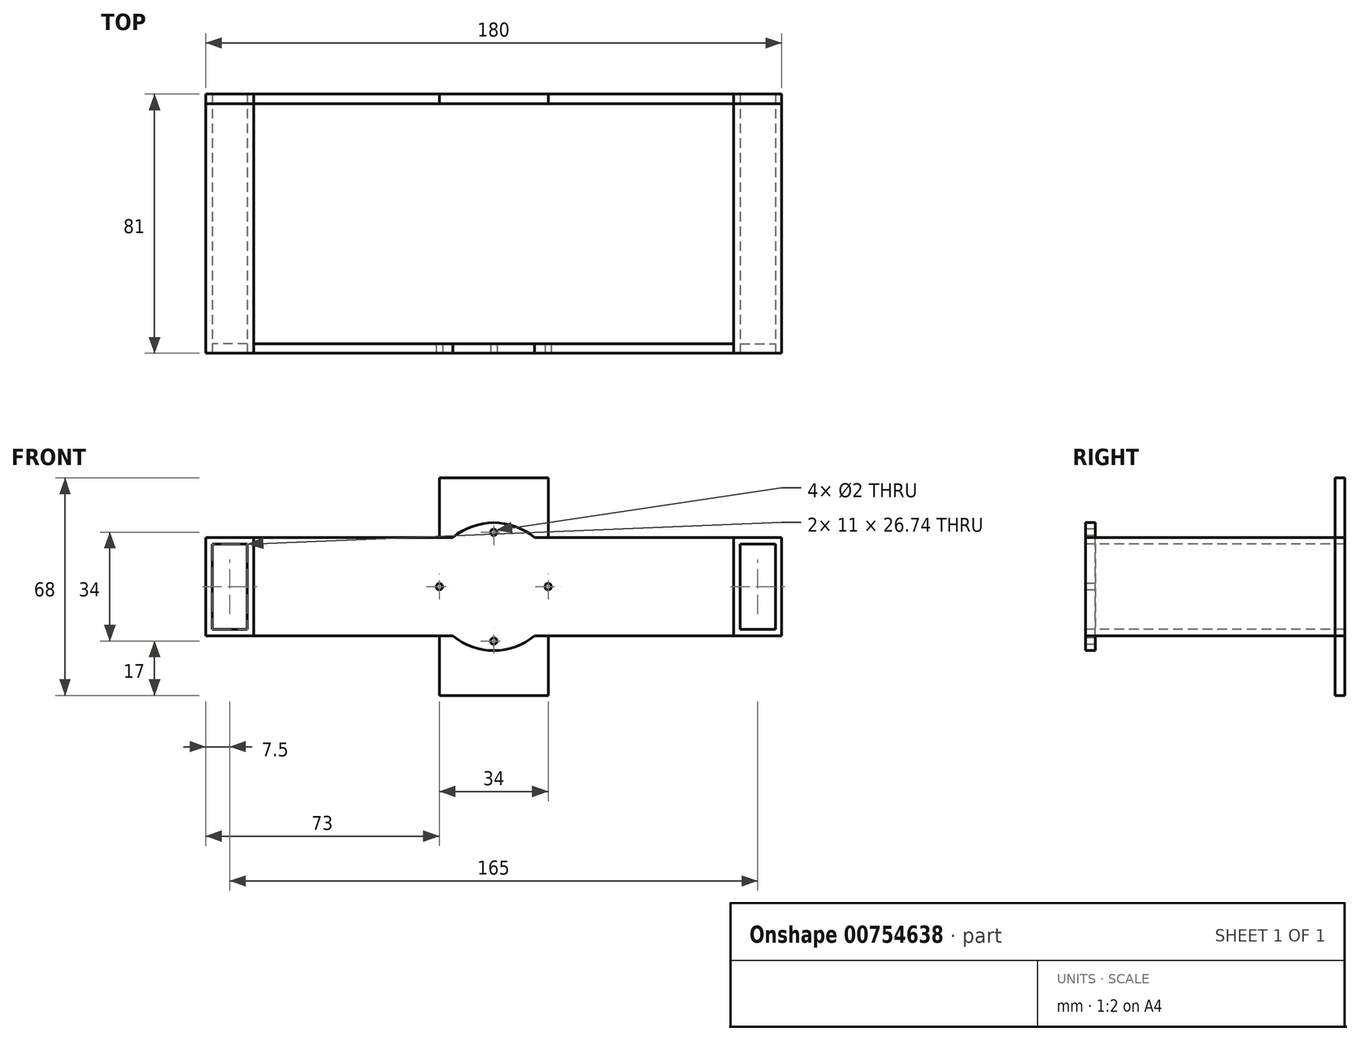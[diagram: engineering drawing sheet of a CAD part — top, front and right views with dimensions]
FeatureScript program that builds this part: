
annotation { "Feature Type Name" : "Feature", "Feature Type Description" : "" }
export const myFeature = defineFeature(function(context is Context, id is Id, definition is map)
    precondition{}
    {
        {
            var Q0;
            Q0=qCreatedBy(makeId("Front.planeOp"),FACE);
            var sketch = newSketch(context, id + "F0", { "sketchPlane" : qUnion([Q0])});
            skCircle(sketch, "E0", {"center": v(0, 0) * mm, "radius": 17 * mm, "construction": true});
            skCircle(sketch, "E1", {"center": v(0, 0) * mm, "radius": 20 * mm});
            skLineSegment(sketch, "E2", {"start": v(0, 0) * mm, "end": v(-69, 0) * mm});
            skLineSegment(sketch, "E3", {"start": v(0, 0) * mm, "end": v(69, 0) * mm});
            skLineSegment(sketch, "E4", {"start": v(-69, 0) * mm, "end": v(-75, 0) * mm});
            skLineSegment(sketch, "E5", {"start": v(69, 0) * mm, "end": v(75, 0) * mm});
            skPoint(sketch, "E6", {"position": v(0, 17) * mm});
            skCircle(sketch, "E7", {"center": v(0, 17) * mm, "radius": 1 * mm});
            skCircle(sketch, "E8.1.0", {"center": v(-17, 0) * mm, "radius": 1 * mm});
            skCircle(sketch, "E8.2.0", {"center": v(0, -17) * mm, "radius": 1 * mm});
            skCircle(sketch, "E8.3.0", {"center": v(17, 0) * mm, "radius": 1 * mm});
            skLineSegment(sketch, "E9", {"start": v(-75, 0) * mm, "end": v(-75, 15.37) * mm});
            skLineSegment(sketch, "E10.MirrorCS", {"start": v(-75, 0) * mm, "end": v(-75, -15.37) * mm});
            skLineSegment(sketch, "E11.MirrorCS", {"start": v(75, 0) * mm, "end": v(75, 15.37) * mm});
            skLineSegment(sketch, "E12.MirrorCS", {"start": v(75, 0) * mm, "end": v(75, -15.37) * mm});
            skLineSegment(sketch, "E13", {"start": v(-75, 15.37) * mm, "end": v(-12.8, 15.37) * mm});
            skLineSegment(sketch, "E14.MirrorCS", {"start": v(-75, -15.37) * mm, "end": v(-12.8, -15.37) * mm});
            skLineSegment(sketch, "E15.MirrorCS", {"start": v(75, 15.37) * mm, "end": v(12.8, 15.37) * mm});
            skLineSegment(sketch, "E16.MirrorCS", {"start": v(75, -15.37) * mm, "end": v(12.8, -15.37) * mm});
            skLineSegment(sketch, "E17", {"start": v(-75, -15.37) * mm, "end": v(-90, -15.37) * mm});
            skLineSegment(sketch, "E18.bottom", {"start": v(-75, 15.37) * mm, "end": v(-90, 15.37) * mm});
            skLineSegment(sketch, "E18.left", {"start": v(-75, 15.37) * mm, "end": v(-75, -15.37) * mm});
            skLineSegment(sketch, "E18.right", {"start": v(-90, 15.37) * mm, "end": v(-90, -15.37) * mm});
            skLineSegment(sketch, "E19.MirrorCS", {"start": v(90, 15.37) * mm, "end": v(90, -15.37) * mm});
            skLineSegment(sketch, "E20.MirrorCS", {"start": v(75, 15.37) * mm, "end": v(90, 15.37) * mm});
            skLineSegment(sketch, "E21.MirrorCS", {"start": v(75, -15.37) * mm, "end": v(90, -15.37) * mm});
            skLineSegment(sketch, "E22.0", {"start": v(-88, 13.37) * mm, "end": v(-88, -13.37) * mm});
            skLineSegment(sketch, "E22.1", {"start": v(-77, 13.37) * mm, "end": v(-88, 13.37) * mm});
            skLineSegment(sketch, "E22.2", {"start": v(-77, -13.37) * mm, "end": v(-88, -13.37) * mm});
            skLineSegment(sketch, "E22.3", {"start": v(-77, 0) * mm, "end": v(-77, -13.37) * mm});
            skLineSegment(sketch, "E22.4", {"start": v(-77, 0) * mm, "end": v(-77, 13.37) * mm});
            skLineSegment(sketch, "E23.MirrorCS", {"start": v(77, 13.37) * mm, "end": v(88, 13.37) * mm});
            skLineSegment(sketch, "E24.MirrorCS", {"start": v(77, -13.37) * mm, "end": v(88, -13.37) * mm});
            skLineSegment(sketch, "E25.MirrorCS", {"start": v(88, 13.37) * mm, "end": v(88, -13.37) * mm});
            skLineSegment(sketch, "E26.MirrorCS", {"start": v(77, 0) * mm, "end": v(77, 13.37) * mm});
            skLineSegment(sketch, "E27.MirrorCS", {"start": v(77, 0) * mm, "end": v(77, -13.37) * mm});
            skSolve(sketch);
        }
        {
            var Q0;
            {var subQ1=sQuery(id+"F0.wireOp",EDGE,"E4");Q0=makeQuery(id+"F0.imprint","IMPRINT",FACE,{"disambiguationData":[TD([[makeQuery(id+"F0.imprint","IMPRINT",EDGE,{"derivedFrom":subQ1}),1.0]])]});}
            var Q1;
            {var subQ4=sQuery(id+"F0.wireOp",EDGE,"E4");Q1=makeQuery(id+"F0.imprint","IMPRINT",FACE,{"disambiguationData":[TD([[makeQuery(id+"F0.imprint","IMPRINT",EDGE,{"derivedFrom":subQ4}),-1.0]])]});}
            var Q2;
            {var subQ4=sQuery(id+"F0.wireOp",EDGE,"E5");Q2=makeQuery(id+"F0.imprint","IMPRINT",FACE,{"disambiguationData":[TD([[makeQuery(id+"F0.imprint","IMPRINT",EDGE,{"derivedFrom":subQ4}),1.0]])]});}
            var Q3;
            {var subQ0=sQuery(id+"F0.wireOp",EDGE,"E5");Q3=makeQuery(id+"F0.imprint","IMPRINT",FACE,{"disambiguationData":[TD([[makeQuery(id+"F0.imprint","IMPRINT",EDGE,{"derivedFrom":subQ0}),-1.0]])]});}
            var Q4;
            Q4=makeQuery(id+"F0.imprint","IMPRINT",FACE,{"disambiguationData":[TD([[makeQuery(id+"F0.imprint","IMPRINT",EDGE,{"derivedFrom":sQuery(id+"F0.wireOp",EDGE,"E7")}),-1.0]])]});
            var Q5;
            Q5=makeQuery(id+"F0.imprint","IMPRINT",FACE,{"disambiguationData":[TD([[makeQuery(id+"F0.imprint","IMPRINT",EDGE,{"derivedFrom":sQuery(id+"F0.wireOp",EDGE,"E8.2.0")}),-1.0]])]});
            extrude(context, id + "F1", {"entities" : qUnion([Q0, Q1, Q2, Q3, Q4, Q5]), "oppositeDirection" : true, "depth" : 3 * mm, "offsetDistance" : 25.4 * mm});
        }
        {
            var Q0;
            Q0=makeQuery(id+"F0.imprint","IMPRINT",FACE,{"disambiguationData":[TD([[makeQuery(id+"F0.imprint","IMPRINT",EDGE,{"derivedFrom":sQuery(id+"F0.wireOp",EDGE,"E11.MirrorCS")}),-1.0]])]});
            var Q1;
            {var subQ3=sQuery(id+"F0.wireOp",EDGE,"E18.bottom");Q1=makeQuery(id+"F0.imprint","IMPRINT",FACE,{"disambiguationData":[TD([[makeQuery(id+"F0.imprint","IMPRINT",EDGE,{"derivedFrom":subQ3}),1.0]])]});}
            extrude(context, id + "F2", {"entities" : qUnion([Q0, Q1]), "oppositeDirection" : true, "depth" : 81 * mm, "offsetDistance" : 25.4 * mm});
        }
        {
            var Q0;
            Q0=qCreatedBy(makeId("Front.planeOp"),FACE);
            cPlane(context, id + "F3", {"entities" : qUnion([Q0]), "cplaneType" : CPlaneType.OFFSET, "offset" : 81 * mm, "oppositeDirection" : true, "width" : 152.4 * mm, "height" : 152.4 * mm});
        }
        {
            var Q0;
            Q0=qCreatedBy(id+"F3.planeOp",FACE);
            var sketch = newSketch(context, id + "F4", { "sketchPlane" : qUnion([Q0])});
            skLineSegment(sketch, "E28", {"start": v(0, 0) * mm, "end": v(-90, 0) * mm});
            skLineSegment(sketch, "E29.MirrorCS", {"start": v(0, 0) * mm, "end": v(90, 0) * mm});
            skLineSegment(sketch, "E30", {"start": v(-90, 0) * mm, "end": v(-90, 15.37) * mm});
            skLineSegment(sketch, "E31.MirrorCS", {"start": v(-90, 0) * mm, "end": v(-90, -15.37) * mm});
            skLineSegment(sketch, "E32.MirrorCS", {"start": v(90, 0) * mm, "end": v(90, 15.37) * mm});
            skLineSegment(sketch, "E33.MirrorCS", {"start": v(90, 0) * mm, "end": v(90, -15.37) * mm});
            skLineSegment(sketch, "E34", {"start": v(90, 15.37) * mm, "end": v(-90, 15.37) * mm});
            skLineSegment(sketch, "E35", {"start": v(90, -15.37) * mm, "end": v(-90, -15.37) * mm});
            skLineSegment(sketch, "E36", {"start": v(0, 0) * mm, "end": v(17, 0) * mm});
            skLineSegment(sketch, "E37.MirrorCS", {"start": v(0, 0) * mm, "end": v(-17, 0) * mm});
            skLineSegment(sketch, "E38", {"start": v(17, 0) * mm, "end": v(17, 34) * mm});
            skLineSegment(sketch, "E39", {"start": v(17, 34) * mm, "end": v(-17, 34) * mm});
            skLineSegment(sketch, "E40", {"start": v(-17, 34) * mm, "end": v(-17, 0) * mm});
            skLineSegment(sketch, "E41.MirrorCS", {"start": v(17, -34) * mm, "end": v(-17, -34) * mm});
            skLineSegment(sketch, "E42.MirrorCS", {"start": v(-17, -34) * mm, "end": v(-17, 0) * mm});
            skLineSegment(sketch, "E43.MirrorCS", {"start": v(17, 0) * mm, "end": v(17, -34) * mm});
            skSolve(sketch);
        }
        {
            var Q0;
            {var subQ3=sQuery(id+"F4.wireOp",EDGE,"E32.MirrorCS");Q0=makeQuery(id+"F4.imprint","IMPRINT",FACE,{"disambiguationData":[TD([[makeQuery(id+"F4.imprint","IMPRINT",EDGE,{"derivedFrom":subQ3}),1.0]])]});}
            var Q1;
            {var subQ3=sQuery(id+"F4.wireOp",EDGE,"E33.MirrorCS");Q1=makeQuery(id+"F4.imprint","IMPRINT",FACE,{"disambiguationData":[TD([[makeQuery(id+"F4.imprint","IMPRINT",EDGE,{"derivedFrom":subQ3}),-1.0]])]});}
            var Q2;
            {var subQ3=sQuery(id+"F4.wireOp",EDGE,"E34");var subQ5=sQuery(id+"F4.wireOp",EDGE,"E40");var subQ6=makeQuery(id+"F4.imprint","INTERSECT",VERTEX,{"derivedFrom":[subQ3,subQ5]});Q2=makeQuery(id+"F4.imprint","IMPRINT",FACE,{"disambiguationData":[TD([[makeQuery(id+"F4.imprint","IMPRINT",EDGE,{"disambiguationData":[TD([[subQ6,1.0]])],"derivedFrom":subQ3}),1.0]])]});}
            var Q3;
            {var subQ5=sQuery(id+"F4.wireOp",EDGE,"E39");Q3=makeQuery(id+"F4.imprint","IMPRINT",FACE,{"disambiguationData":[TD([[makeQuery(id+"F4.imprint","IMPRINT",EDGE,{"derivedFrom":subQ5}),1.0]])]});}
            var Q4;
            {var subQ0=sQuery(id+"F4.wireOp",EDGE,"E42.MirrorCS");var subQ1=sQuery(id+"F4.wireOp",EDGE,"E35");var subQ2=makeQuery(id+"F4.imprint","INTERSECT",VERTEX,{"derivedFrom":[subQ1,subQ0]});Q4=makeQuery(id+"F4.imprint","IMPRINT",FACE,{"disambiguationData":[TD([[makeQuery(id+"F4.imprint","IMPRINT",EDGE,{"disambiguationData":[TD([[subQ2,1.0]])],"derivedFrom":subQ1}),-1.0]])]});}
            var Q5;
            {var subQ5=sQuery(id+"F4.wireOp",EDGE,"E41.MirrorCS");Q5=makeQuery(id+"F4.imprint","IMPRINT",FACE,{"disambiguationData":[TD([[makeQuery(id+"F4.imprint","IMPRINT",EDGE,{"derivedFrom":subQ5}),-1.0]])]});}
            var Q6;
            {var subQ3=sQuery(id+"F4.wireOp",EDGE,"E31.MirrorCS");Q6=makeQuery(id+"F4.imprint","IMPRINT",FACE,{"disambiguationData":[TD([[makeQuery(id+"F4.imprint","IMPRINT",EDGE,{"derivedFrom":subQ3}),1.0]])]});}
            var Q7;
            {var subQ3=sQuery(id+"F4.wireOp",EDGE,"E30");Q7=makeQuery(id+"F4.imprint","IMPRINT",FACE,{"disambiguationData":[TD([[makeQuery(id+"F4.imprint","IMPRINT",EDGE,{"derivedFrom":subQ3}),-1.0]])]});}
            extrude(context, id + "F5", {"entities" : qUnion([Q0, Q1, Q2, Q3, Q4, Q5, Q6, Q7]), "depth" : 3 * mm, "offsetDistance" : 25.4 * mm});
        }
        {
            var Q0;
            Q0=makeQuery(id+"F0.imprint","IMPRINT",FACE,{"disambiguationData":[TD([[makeQuery(id+"F0.imprint","IMPRINT",EDGE,{"derivedFrom":sQuery(id+"F0.wireOp",EDGE,"E23.MirrorCS")}),-1.0]])]});
            var Q1;
            Q1=makeQuery(id+"F0.imprint","IMPRINT",FACE,{"disambiguationData":[TD([[makeQuery(id+"F0.imprint","IMPRINT",EDGE,{"derivedFrom":sQuery(id+"F0.wireOp",EDGE,"E22.0")}),1.0]])]});
            extrude(context, id + "F6", {"entities" : qUnion([Q0, Q1]), "oppositeDirection" : true, "depth" : 3 * mm, "offsetDistance" : 25.4 * mm});
        }
    });
